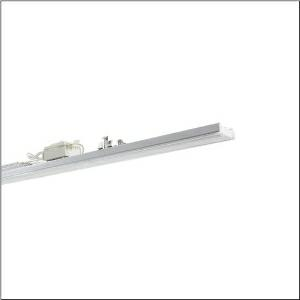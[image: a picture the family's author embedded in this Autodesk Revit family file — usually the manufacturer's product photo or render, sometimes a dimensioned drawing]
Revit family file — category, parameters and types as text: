
# Revit family: licross_r__21_recessed_mo_52te19dn495g_53e3
name_source: partatom
category: Lighting Fixtures
units: mm (PartAtom-declared; Revit-internal decimal feet)

## family parameters
Cut with Voids When Loaded = No
Host = Face
Light Source = No
Part Type = Normal
Room Calculation Point = No
Round Connector Dimension = Use Diameter
Shared = No

## types (1)
- --- (1 x LED, 9850 lm, 58 W, 4000K)
    Apparent Load = 58 VA
    CIE Flux Codes = 55 90 98 100 100
    Color Rendering = 80
    Color Temperature = 4000K
    Default Elevation = 1800 mm
    Description = Licross® 21 Recessed MO, luminaire insert, of sheet steel, galvanised, coil coated, white, length: 1.500mm, width: 66mm, height: 67mm, LED rated luminous flux: 9.850lm, light colour: 840, control gear: DALI 2, with plug, 5-pole, with phase selection, mains connection: 220..240V, AC, 50/60Hz, rated input power: 58W, halogen-free wiring, primary light control with lens, of plastic, primary optical cover: cover, of PMMA, light emission: direct distribution, primary light characteristic: double asymmetric, protection rating (complete): IP54, insulation class (complete): insulation class I (protective earthing), certification: CE, ENEC, VDE, UKCA, protection symbol: D if used in an environment with non-conductive dust loads with corresponding accessories, impact resistance: IK06, permissible ambient temperature for indoor applications: -25..+35°C, corresponds to IFS (International Featured Standards) requirements for safety and quality in the food industry, reducing of maximum allowable ambient temperature of 5°C with ceiling mounting, LABS conformity tested according to VDMA 24364:2018-05, packaging unit: 1 piece
    Height = 58 mm
    Lamp = 1 x LED
    Lamp Light Flux = 9850 lm
    Lamp Power = 58 W
    Lamp count = 1
    Length = 1500 mm
    Luminous efficacy = 170 lm/W
    Manufacturer = Siteco
    ModVariant = No
    Model = 52TE19DN495G
    Mounting Place = Ceiling
    Mounting Type = Pendant
    Number of Poles = 1
    OnlyDefault = Yes
    Power Factor = 1
    Product Name = Licross® 21 Recessed MO
    Product group = luminaire insert
    ProductGroupID = 902
    Protection Class = Protection class I
    Protection Degree = IP 54
    RLX_Detail_Level = 1
    RLX_Emergency_Light_Flux = 0 lm
    RLX_Emergency_Type = 0
    RLX_Emergency_Type_DB = No
    RlxData = <blob elided: 24549 chars, md5=0bb02efb>
    Socket = socket
    Standby Power = 0 W
    System Light Flux = 9850 lm
    System Power = 58 W
    Type Comments = factory setting: luminous flux: 100 % | dim-lin: 254 | 390 mA
    Type Image = l_1296930.jpg
    URL = http://relux.com
    VarID = @adj_127924
    Voltage = 0 V
    Weight = 0.00 kg
    Width = 66 mm

## geometry (parser evidence)
native form markers: Blend x4, Sweep x10
no freeform markers — native parametric forms only
